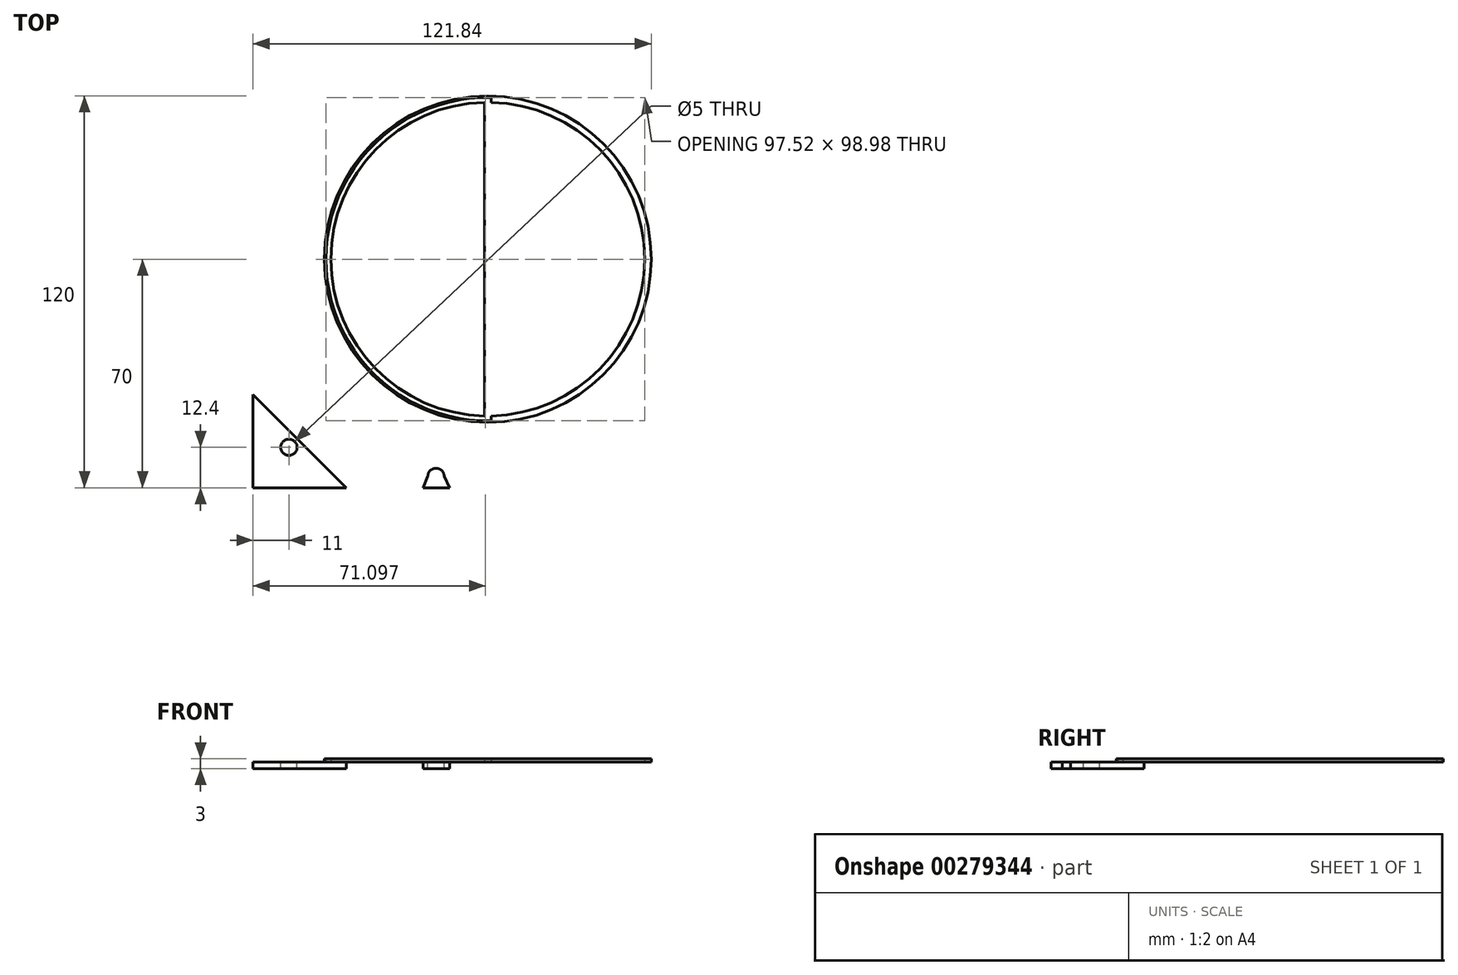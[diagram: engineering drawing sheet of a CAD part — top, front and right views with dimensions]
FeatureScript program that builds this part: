
annotation { "Feature Type Name" : "Feature", "Feature Type Description" : "" }
export const myFeature = defineFeature(function(context is Context, id is Id, definition is map)
    precondition{}
    {
        {
            var Q0;
            Q0=qCreatedBy(makeId("Top.planeOp"),FACE);
            var sketch = newSketch(context, id + "F0", { "sketchPlane" : qUnion([Q0])});
            skLineSegment(sketch, "E0.bottom", {"start": v(75, 70) * mm, "end": v(-75, 70) * mm});
            skLineSegment(sketch, "E0.top", {"start": v(75, -70) * mm, "end": v(-75, -70) * mm});
            skLineSegment(sketch, "E0.left", {"start": v(75, 70) * mm, "end": v(75, -70) * mm});
            skLineSegment(sketch, "E0.right", {"start": v(-75, 70) * mm, "end": v(-75, -70) * mm});
            skPoint(sketch, "E0.middle", {"position": v(0, 0) * mm});
            skSolve(sketch);
        }
        {
            var Q0;
            Q0=qSketchRegion(id+"F0",true);
            extrude(context, id + "F1", {"entities" : qUnion([Q0]), "depth" : 2 * mm});
        }
        {
            var Q0;
            Q0=makeQuery(id+"F1.opExtrude","CAP_FACE",FACE,{"disambiguationData":[OSD([sQuery(id+"F0.wireOp",EDGE,"E0.bottom"),sQuery(id+"F0.wireOp",EDGE,"E0.top"),sQuery(id+"F0.wireOp",EDGE,"E0.left"),sQuery(id+"F0.wireOp",EDGE,"E0.right")])],"isStart":false});
            var sketch = newSketch(context, id + "F2", { "sketchPlane" : qUnion([Q0])});
            skArc(sketch, "E1", {"start": v(-67.18, 6.35) * mm, "mid": v(-67.92, 8.12) * mm, "end": v(-69.68, 8.85) * mm});
            skArc(sketch, "E2.MirrorC", {"start": v(-67.18, -6.35) * mm, "mid": v(-67.92, -8.12) * mm, "end": v(-69.68, -8.85) * mm});
            skArc(sketch, "E3", {"start": v(-21.5, 66.52) * mm, "mid": v(-19, 64) * mm, "end": v(-16.5, 66.52) * mm});
            skCircle(sketch, "E4", {"center": v(-64, 57.6) * mm, "radius": 2.5 * mm});
            skArc(sketch, "E5.MirrorC", {"start": v(-21.5, -66.52) * mm, "mid": v(-19, -64) * mm, "end": v(-16.5, -66.52) * mm});
            skCircle(sketch, "E6.MirrorC", {"center": v(-64, -57.6) * mm, "radius": 2.5 * mm});
            skLineSegment(sketch, "E7", {"start": v(-21.5, 66.52) * mm, "end": v(-22.94, 70) * mm});
            skLineSegment(sketch, "E8.MirrorCS", {"start": v(-16.5, 66.52) * mm, "end": v(-14.88, 70) * mm});
            skLineSegment(sketch, "E9.MirrorCS", {"start": v(-16.5, -66.52) * mm, "end": v(-14.88, -70) * mm});
            skLineSegment(sketch, "E10.MirrorCS", {"start": v(-21.5, -66.52) * mm, "end": v(-22.94, -70) * mm});
            skLineSegment(sketch, "E11", {"start": v(-46.5, 70) * mm, "end": v(-75, 41.5) * mm});
            skLineSegment(sketch, "E12.MirrorCS", {"start": v(-46.5, -70) * mm, "end": v(-75, -41.5) * mm});
            skLineSegment(sketch, "E13", {"start": v(-69.68, 8.85) * mm, "end": v(-75, 8.85) * mm});
            skLineSegment(sketch, "E14", {"start": v(-67.18, -6.35) * mm, "end": v(-67.18, 6.35) * mm});
            skLineSegment(sketch, "E15.MirrorCS", {"start": v(-69.68, -8.85) * mm, "end": v(-75, -8.85) * mm});
            skSolve(sketch);
        }
        {
            var Q0;
            Q0=qSketchRegion(id+"F2",true);
            var Q1;
            Q1=makeQuery(id+"F2.imprint","IMPRINT",FACE,{"disambiguationData":[TD([[makeQuery(id+"F2.imprint","IMPRINT",EDGE,{"derivedFrom":sQuery(id+"F2.wireOp",EDGE,"E4")}),-1.0]])]});
            var Q2;
            Q2=makeQuery(id+"F2.imprint","IMPRINT",FACE,{"disambiguationData":[TD([[makeQuery(id+"F2.imprint","IMPRINT",EDGE,{"derivedFrom":sQuery(id+"F2.wireOp",EDGE,"E1")}),1.0]])]});
            var Q3;
            Q3=makeQuery(id+"F2.imprint","IMPRINT",FACE,{"disambiguationData":[TD([[makeQuery(id+"F2.imprint","IMPRINT",EDGE,{"derivedFrom":sQuery(id+"F2.wireOp",EDGE,"E5.MirrorC")}),-1.0]])]});
            var Q4;
            Q4=makeQuery(id+"F2.imprint","IMPRINT",FACE,{"disambiguationData":[TD([[makeQuery(id+"F2.imprint","IMPRINT",EDGE,{"derivedFrom":sQuery(id+"F2.wireOp",EDGE,"E3")}),1.0]])]});
            var Q5;
            Q5=makeQuery(id+"F2.imprint","IMPRINT",FACE,{"disambiguationData":[TD([[makeQuery(id+"F2.imprint","IMPRINT",EDGE,{"derivedFrom":sQuery(id+"F2.wireOp",EDGE,"E6.MirrorC")}),1.0]])]});
            extrude(context, id + "F3", {"entities" : qUnion([Q0, Q1, Q2, Q3, Q4, Q5]), "operationType" : NewBodyOperationType.REMOVE, "oppositeDirection" : true, "depth" : 5 * mm});
        }
        {
            var Q0;
            Q0=makeQuery(id+"F1.opExtrude","CAP_FACE",FACE,{"disambiguationData":[OSD([sQuery(id+"F0.wireOp",EDGE,"E0.bottom"),sQuery(id+"F0.wireOp",EDGE,"E0.top"),sQuery(id+"F0.wireOp",EDGE,"E0.left"),sQuery(id+"F0.wireOp",EDGE,"E0.right")])],"isStart":false});
            var sketch = newSketch(context, id + "F4", { "sketchPlane" : qUnion([Q0])});
            skCircle(sketch, "E16", {"center": v(-3.16, 0) * mm, "radius": 50 * mm});
            skCircle(sketch, "E17", {"center": v(-3.16, 0) * mm, "radius": 49.5 * mm});
            skCircle(sketch, "E18", {"center": v(-3.16, 0) * mm, "radius": 49.75 * mm});
            skPoint(sketch, "E19", {"position": v(-4.16, 49.74) * mm});
            skLineSegment(sketch, "E20", {"start": v(-4.16, 49.74) * mm, "end": v(-4.16, -54.84) * mm});
            skLineSegment(sketch, "E21", {"start": v(-2.16, 49.74) * mm, "end": v(-2.16, -49.74) * mm});
            skArc(sketch, "E22", {"start": v(-4.16, 48) * mm, "mid": v(-51.16, 0) * mm, "end": v(-4.16, -48) * mm});
            skLineSegment(sketch, "E23", {"start": v(-3.15, 52.88) * mm, "end": v(-3.15, -64.17) * mm});
            skLineSegment(sketch, "E24.MirrorCS", {"start": v(-2.14, 49.74) * mm, "end": v(-2.14, -54.84) * mm});
            skArc(sketch, "E25.MirrorCS", {"start": v(-2.14, 48) * mm, "mid": v(44.86, 0) * mm, "end": v(-2.14, -48) * mm});
            skSolve(sketch);
        }
        {
            var Q0;
            {var subQ0=sQuery(id+"F4.wireOp",EDGE,"E22");Q0=makeQuery(id+"F4.imprint","IMPRINT",FACE,{"disambiguationData":[TD([[makeQuery(id+"F4.imprint","IMPRINT",EDGE,{"derivedFrom":subQ0}),1.0]])]});}
            var Q1;
            {var subQ0=sQuery(id+"F4.wireOp",EDGE,"E20");var subQ1=sQuery(id+"F4.wireOp",EDGE,"E17");var subQ2=makeQuery(id+"F4.imprint","INTERSECT",VERTEX,{"disambiguationData":[OD(0.0)],"derivedFrom":[subQ1,subQ0]});Q1=makeQuery(id+"F4.imprint","IMPRINT",FACE,{"disambiguationData":[TD([[makeQuery(id+"F4.imprint","IMPRINT",EDGE,{"disambiguationData":[TD([[subQ2,-1.0]])],"derivedFrom":subQ1}),-1.0]])]});}
            var Q2;
            {var subQ0=sQuery(id+"F4.wireOp",EDGE,"E20");var subQ6=sQuery(id+"F4.wireOp",EDGE,"E16");var subQ7=makeQuery(id+"F4.imprint","INTERSECT",VERTEX,{"derivedFrom":[subQ6,subQ0]});Q2=makeQuery(id+"F4.imprint","IMPRINT",FACE,{"disambiguationData":[TD([[makeQuery(id+"F4.imprint","IMPRINT",EDGE,{"disambiguationData":[TD([[subQ7,1.0]])],"derivedFrom":subQ6}),1.0]])]});}
            var Q3;
            {var subQ0=sQuery(id+"F4.wireOp",EDGE,"E25.MirrorCS");Q3=makeQuery(id+"F4.imprint","IMPRINT",FACE,{"disambiguationData":[TD([[makeQuery(id+"F4.imprint","IMPRINT",EDGE,{"derivedFrom":subQ0}),-1.0]])]});}
            var Q4;
            {var subQ2=sQuery(id+"F4.wireOp",EDGE,"E23");var subQ7=sQuery(id+"F4.wireOp",EDGE,"E16");var subQ8=makeQuery(id+"F4.imprint","INTERSECT",VERTEX,{"disambiguationData":[OD(0.0)],"derivedFrom":[subQ7,subQ2]});Q4=makeQuery(id+"F4.imprint","IMPRINT",FACE,{"disambiguationData":[TD([[makeQuery(id+"F4.imprint","IMPRINT",EDGE,{"disambiguationData":[TD([[subQ8,1.0]])],"derivedFrom":subQ7}),1.0]])]});}
            var Q5;
            {var subQ0=sQuery(id+"F4.wireOp",EDGE,"E24.MirrorCS");var subQ1=sQuery(id+"F4.wireOp",EDGE,"E17");var subQ2=makeQuery(id+"F4.imprint","INTERSECT",VERTEX,{"disambiguationData":[OD(0.0)],"derivedFrom":[subQ1,subQ0]});Q5=makeQuery(id+"F4.imprint","IMPRINT",FACE,{"disambiguationData":[TD([[makeQuery(id+"F4.imprint","IMPRINT",EDGE,{"disambiguationData":[TD([[subQ2,1.0]])],"derivedFrom":subQ1}),-1.0]])]});}
            var Q6;
            {var subQ0=sQuery(id+"F4.wireOp",EDGE,"E20");var subQ1=sQuery(id+"F4.wireOp",EDGE,"E16");var subQ2=makeQuery(id+"F4.imprint","INTERSECT",VERTEX,{"derivedFrom":[subQ1,subQ0]});Q6=makeQuery(id+"F4.imprint","IMPRINT",FACE,{"disambiguationData":[TD([[makeQuery(id+"F4.imprint","IMPRINT",EDGE,{"disambiguationData":[TD([[subQ2,-1.0]])],"derivedFrom":subQ1}),1.0]])]});}
            var Q7;
            {var subQ0=sQuery(id+"F4.wireOp",EDGE,"E23");var subQ1=sQuery(id+"F4.wireOp",EDGE,"E16");var subQ2=makeQuery(id+"F4.imprint","INTERSECT",VERTEX,{"disambiguationData":[OD(1.0)],"derivedFrom":[subQ1,subQ0]});Q7=makeQuery(id+"F4.imprint","IMPRINT",FACE,{"disambiguationData":[TD([[makeQuery(id+"F4.imprint","IMPRINT",EDGE,{"disambiguationData":[TD([[subQ2,-1.0]])],"derivedFrom":subQ1}),1.0]])]});}
            var Q8;
            {var subQ0=sQuery(id+"F4.wireOp",EDGE,"E23");var subQ1=sQuery(id+"F4.wireOp",EDGE,"E17");var subQ2=makeQuery(id+"F4.imprint","INTERSECT",VERTEX,{"disambiguationData":[OD(1.0)],"derivedFrom":[subQ1,subQ0]});Q8=makeQuery(id+"F4.imprint","IMPRINT",FACE,{"disambiguationData":[TD([[makeQuery(id+"F4.imprint","IMPRINT",EDGE,{"disambiguationData":[TD([[subQ2,-1.0]])],"derivedFrom":subQ1}),-1.0]])]});}
            var Q9;
            {var subQ0=sQuery(id+"F4.wireOp",EDGE,"E20");var subQ1=sQuery(id+"F4.wireOp",EDGE,"E17");var subQ2=makeQuery(id+"F4.imprint","INTERSECT",VERTEX,{"disambiguationData":[OD(1.0)],"derivedFrom":[subQ1,subQ0]});Q9=makeQuery(id+"F4.imprint","IMPRINT",FACE,{"disambiguationData":[TD([[makeQuery(id+"F4.imprint","IMPRINT",EDGE,{"disambiguationData":[TD([[subQ2,-1.0]])],"derivedFrom":subQ1}),-1.0]])]});}
            var Q10;
            {var subQ0=sQuery(id+"F4.wireOp",EDGE,"E21");var subQ1=sQuery(id+"F4.wireOp",EDGE,"E17");var subQ2=makeQuery(id+"F4.imprint","INTERSECT",VERTEX,{"disambiguationData":[OD(1.0)],"derivedFrom":[subQ1,subQ0]});Q10=makeQuery(id+"F4.imprint","IMPRINT",FACE,{"disambiguationData":[TD([[makeQuery(id+"F4.imprint","IMPRINT",EDGE,{"disambiguationData":[TD([[subQ2,-1.0]])],"derivedFrom":subQ1}),-1.0]])]});}
            var Q11;
            {var subQ0=sQuery(id+"F4.wireOp",EDGE,"E21");var subQ1=sQuery(id+"F4.wireOp",EDGE,"E17");var subQ2=makeQuery(id+"F4.imprint","INTERSECT",VERTEX,{"disambiguationData":[OD(0.0)],"derivedFrom":[subQ1,subQ0]});Q11=makeQuery(id+"F4.imprint","IMPRINT",FACE,{"disambiguationData":[TD([[makeQuery(id+"F4.imprint","IMPRINT",EDGE,{"disambiguationData":[TD([[subQ2,-1.0]])],"derivedFrom":subQ1}),-1.0]])]});}
            var Q12;
            {var subQ0=sQuery(id+"F4.wireOp",EDGE,"E23");var subQ1=sQuery(id+"F4.wireOp",EDGE,"E17");var subQ2=makeQuery(id+"F4.imprint","INTERSECT",VERTEX,{"disambiguationData":[OD(0.0)],"derivedFrom":[subQ1,subQ0]});Q12=makeQuery(id+"F4.imprint","IMPRINT",FACE,{"disambiguationData":[TD([[makeQuery(id+"F4.imprint","IMPRINT",EDGE,{"disambiguationData":[TD([[subQ2,-1.0]])],"derivedFrom":subQ1}),-1.0]])]});}
            var Q13;
            {var subQ0=sQuery(id+"F4.wireOp",EDGE,"E21");var subQ1=sQuery(id+"F4.wireOp",EDGE,"E17");var subQ2=makeQuery(id+"F4.imprint","INTERSECT",VERTEX,{"disambiguationData":[OD(0.0)],"derivedFrom":[subQ1,subQ0]});Q13=makeQuery(id+"F4.imprint","IMPRINT",FACE,{"disambiguationData":[TD([[makeQuery(id+"F4.imprint","IMPRINT",EDGE,{"disambiguationData":[TD([[subQ2,1.0]])],"derivedFrom":subQ1}),-1.0]])]});}
            extrude(context, id + "F5", {"entities" : qUnion([Q0, Q1, Q2, Q3, Q4, Q5, Q6, Q7, Q8, Q9, Q10, Q11, Q12, Q13]), "depth" : 1 * mm});
        }
    });
